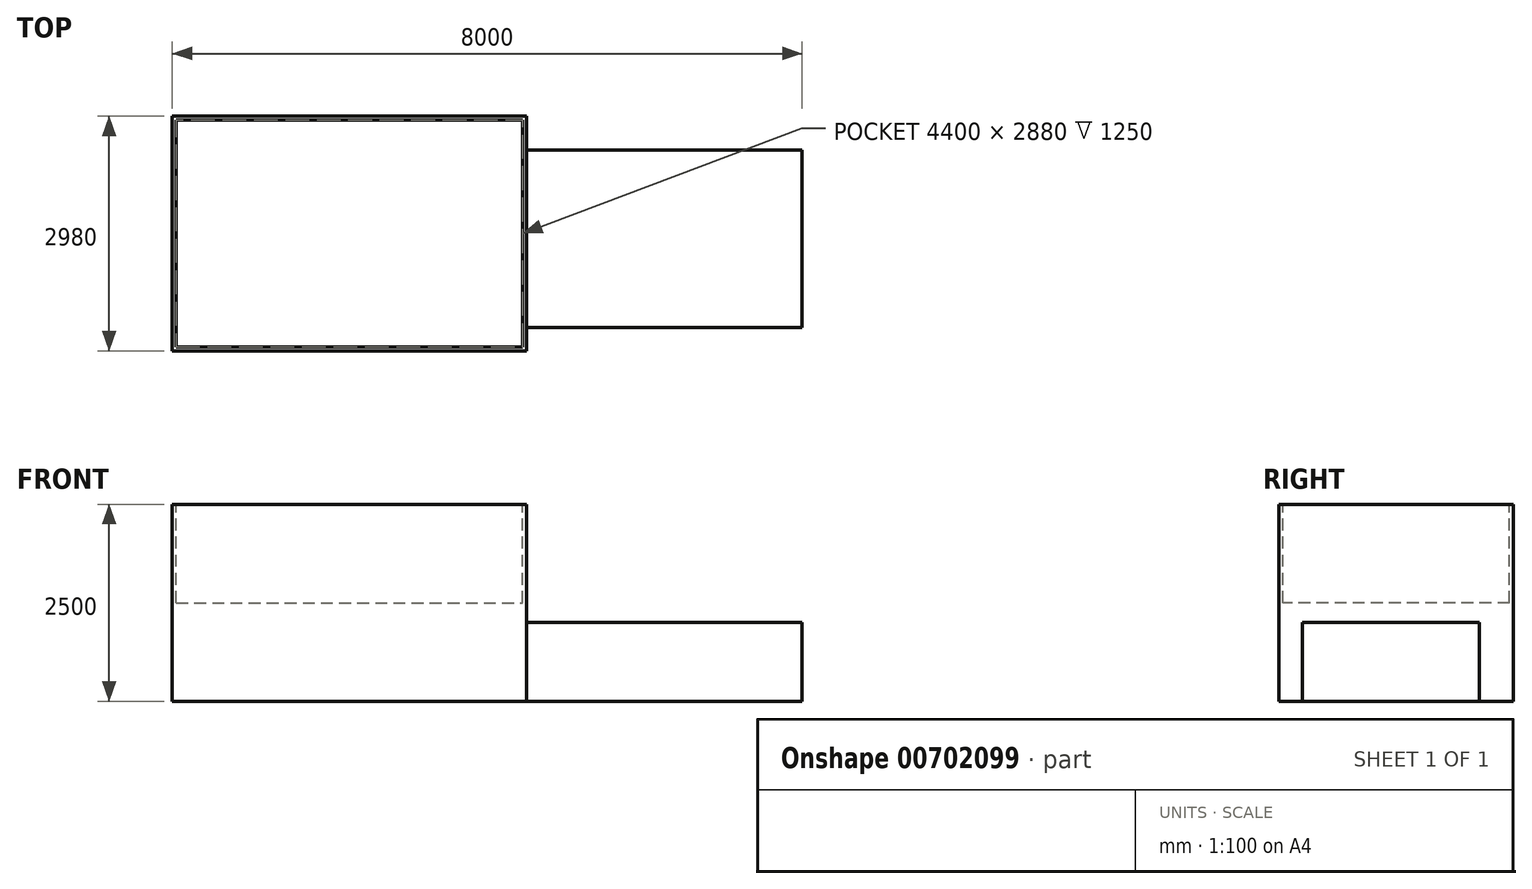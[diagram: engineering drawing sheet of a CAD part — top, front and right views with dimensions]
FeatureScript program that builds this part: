
annotation { "Feature Type Name" : "Feature", "Feature Type Description" : "" }
export const myFeature = defineFeature(function(context is Context, id is Id, definition is map)
    precondition{}
    {
        {
            var Q0;
            Q0=qCreatedBy(makeId("Top.planeOp"),FACE);
            var sketch = newSketch(context, id + "F0", { "sketchPlane" : qUnion([Q0])});
            skLineSegment(sketch, "E0.bottom", {"start": v(0, 0) * mm, "end": v(4500, 0) * mm});
            skLineSegment(sketch, "E0.top", {"start": v(0, 2980) * mm, "end": v(4500, 2980) * mm});
            skLineSegment(sketch, "E0.left", {"start": v(0, 0) * mm, "end": v(0, 2980) * mm});
            skLineSegment(sketch, "E0.right", {"start": v(4500, 0) * mm, "end": v(4500, 2980) * mm});
            skSolve(sketch);
        }
        {
            var Q0;
            Q0=makeQuery(id+"F0.imprint","IMPRINT",FACE,{"disambiguationData":[TD([[makeQuery(id+"F0.imprint","IMPRINT",EDGE,{"derivedFrom":sQuery(id+"F0.wireOp",EDGE,"E0.bottom")}),1.0]])]});
            extrude(context, id + "F1", {"entities" : qUnion([Q0]), "depth" : 2500 * mm, "offsetDistance" : 25 * mm});
        }
        {
            var Q0;
            Q0=makeQuery(id+"F1.opExtrude","CAP_FACE",FACE,{"disambiguationData":[OSD([sQuery(id+"F0.wireOp",EDGE,"E0.bottom"),sQuery(id+"F0.wireOp",EDGE,"E0.top"),sQuery(id+"F0.wireOp",EDGE,"E0.left"),sQuery(id+"F0.wireOp",EDGE,"E0.right")])],"isStart":false});
            var sketch = newSketch(context, id + "F2", { "sketchPlane" : qUnion([Q0])});
            skLineSegment(sketch, "E1.bottom", {"start": v(50, 2930) * mm, "end": v(4450, 2930) * mm});
            skLineSegment(sketch, "E1.top", {"start": v(50, 50) * mm, "end": v(4450, 50) * mm});
            skLineSegment(sketch, "E1.left", {"start": v(50, 2930) * mm, "end": v(50, 50) * mm});
            skLineSegment(sketch, "E1.right", {"start": v(4450, 2930) * mm, "end": v(4450, 50) * mm});
            skSolve(sketch);
        }
        {
            var Q0;
            Q0=makeQuery(id+"F2.imprint","IMPRINT",FACE,{"disambiguationData":[TD([[makeQuery(id+"F2.imprint","IMPRINT",EDGE,{"derivedFrom":sQuery(id+"F2.wireOp",EDGE,"E1.bottom")}),-1.0]])]});
            extrude(context, id + "F3", {"entities" : qUnion([Q0]), "operationType" : NewBodyOperationType.REMOVE, "oppositeDirection" : true, "depth" : 1250 * mm, "offsetDistance" : 25 * mm});
        }
        {
            var Q0;
            Q0=makeQuery(id+"F1.opExtrude","SWEPT_FACE",FACE,{"disambiguationData":[OSD([sQuery(id+"F0.wireOp",EDGE,"E0.right")])]});
            var sketch = newSketch(context, id + "F4", { "sketchPlane" : qUnion([Q0])});
            skLineSegment(sketch, "E2.bottom", {"start": v(300, 0) * mm, "end": v(2550, 0) * mm});
            skLineSegment(sketch, "E2.top", {"start": v(300, 1000) * mm, "end": v(2550, 1000) * mm});
            skLineSegment(sketch, "E2.left", {"start": v(300, 0) * mm, "end": v(300, 1000) * mm});
            skLineSegment(sketch, "E2.right", {"start": v(2550, 0) * mm, "end": v(2550, 1000) * mm});
            skSolve(sketch);
        }
        {
            var Q0;
            Q0=makeQuery(id+"F4.imprint","IMPRINT",FACE,{"disambiguationData":[TD([[makeQuery(id+"F4.imprint","IMPRINT",EDGE,{"derivedFrom":sQuery(id+"F4.wireOp",EDGE,"E2.bottom")}),1.0]])]});
            extrude(context, id + "F5", {"entities" : qUnion([Q0]), "operationType" : NewBodyOperationType.ADD, "depth" : 3500 * mm, "offsetDistance" : 25 * mm});
        }
    });
